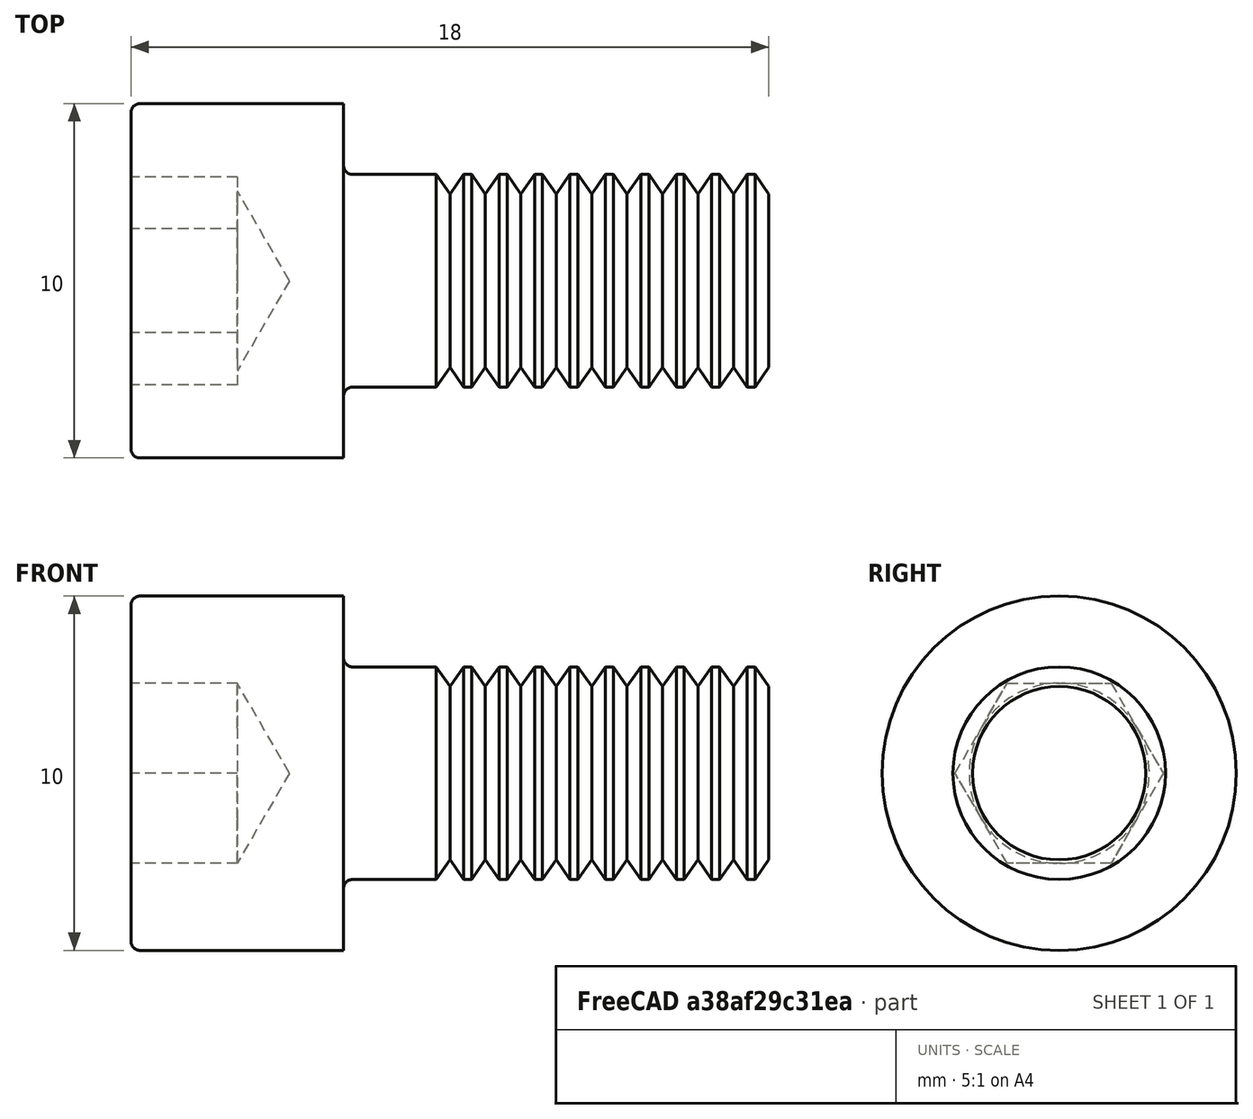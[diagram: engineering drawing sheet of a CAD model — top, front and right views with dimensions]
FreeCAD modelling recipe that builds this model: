
FCSTD DOCUMENT  (FreeCAD 0.21R33771 (Git))
Label: m6x12_screw
License: All rights reserved
LicenseURL: http://en.wikipedia.org/wiki/All_rights_reserved
objects: Part::Feature×1, Sketcher::SketchObject×1, PartDesign::FeatureBase×1, PartDesign::Pocket×1, PartDesign::Body×1
note: 6 computed .brp shape members not serialized (recipe doc carries the construction recipe); baked Part::Feature solids carry a one-line shape summary decoded from their .brp

FEATURE [Part::Feature] Part__Feature004  label="m6"
  shape: bbox 26 x 10.82 x 10.82 mm, 129 faces (baked)
FEATURE [Sketcher::SketchObject] Sketch
  FullyConstrained = false
  MapMode = 5
  Placement = pos=(15.8921,0,0) rot=(0.57735,0.57735,0.57735;2.0944rad)
  Support = -> [Part__Feature004]
  sketch-geometry (1):
    g0: Circle CenterX=0 CenterY=0 CenterZ=0 NormalX=0 NormalY=0 NormalZ=1 AngleXU=0 Radius=9.23049
  constraints (1):
    c: Coincident(g0,g-1)
FEATURE [PartDesign::FeatureBase] BaseFeature
  BaseFeature = -> Part__Feature004
FEATURE [PartDesign::Pocket] Pocket
  BaseFeature = -> BaseFeature
  Direction = (-1,0,0)
  Length = 8
  Length2 = 5
  Profile = -> Sketch
  ReferenceAxis = -> Sketch [N_Axis]
  Refine = true
  Type = 0
FEATURE [PartDesign::Body] Body
  BaseFeature = -> Part__Feature004
  Group = -> [BaseFeature,Sketch,Pocket]
  Origin = -> Origin
  Tip = -> Pocket
